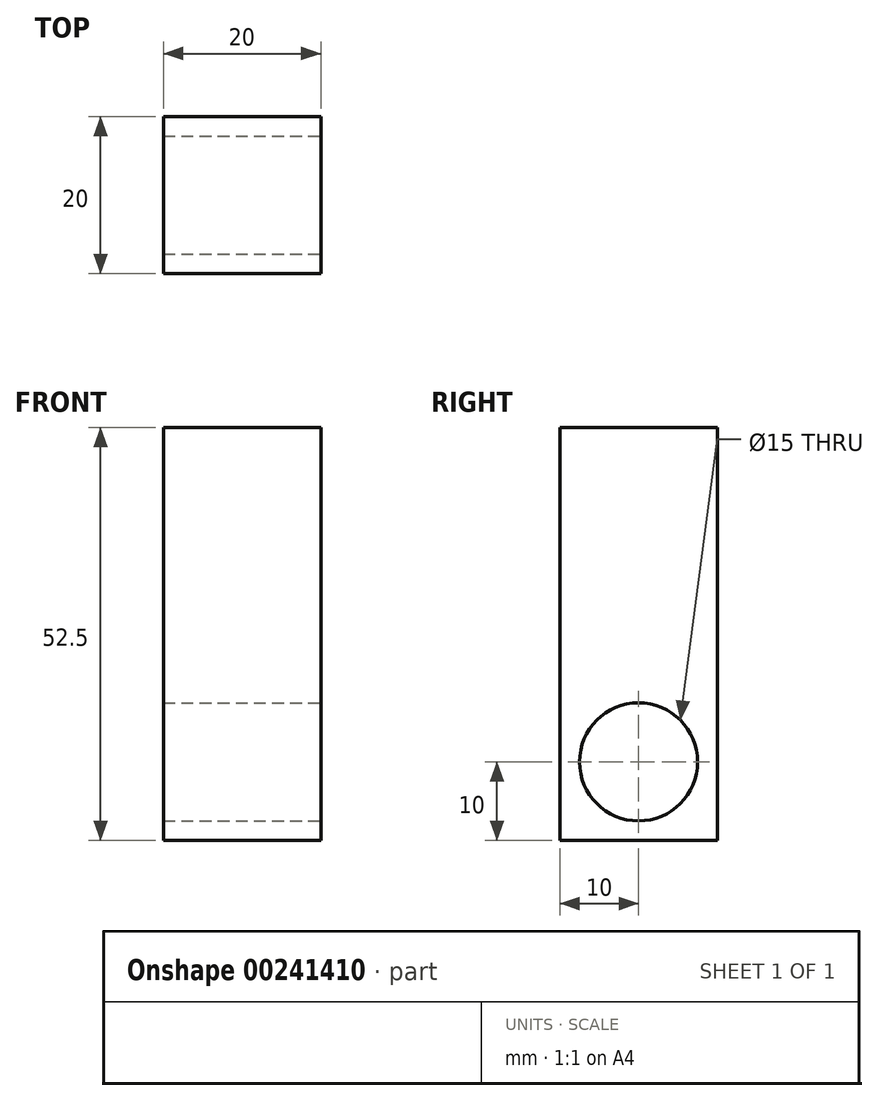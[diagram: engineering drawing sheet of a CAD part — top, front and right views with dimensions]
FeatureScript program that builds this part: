
annotation { "Feature Type Name" : "Feature", "Feature Type Description" : "" }
export const myFeature = defineFeature(function(context is Context, id is Id, definition is map)
    precondition{}
    {
        {
            var Q0;
            Q0=qCreatedBy(makeId("Right.planeOp"),FACE);
            var sketch = newSketch(context, id + "F0", { "sketchPlane" : qUnion([Q0])});
            skLineSegment(sketch, "E0.bottom", {"start": v(-10, 10) * mm, "end": v(10, 10) * mm});
            skLineSegment(sketch, "E0.top", {"start": v(-10, -10) * mm, "end": v(10, -10) * mm});
            skLineSegment(sketch, "E0.left", {"start": v(-10, 10) * mm, "end": v(-10, -10) * mm});
            skLineSegment(sketch, "E0.right", {"start": v(10, 10) * mm, "end": v(10, -10) * mm});
            skPoint(sketch, "E0.middle", {"position": v(0, 0) * mm});
            skSolve(sketch);
        }
        {
            var Q0;
            Q0 = qSketchRegion(id + "F0", true);
            extrude(context, id + "F1", {"entities" : qUnion([Q0]), "depth" : 20 * mm});
        }
        {
            var Q0;
            Q0=makeQuery(id+"F1.opExtrude","CAP_FACE",FACE,{"disambiguationData":[OSD([sQuery(id+"F0.wireOp",EDGE,"E0.bottom"),sQuery(id+"F0.wireOp",EDGE,"E0.top"),sQuery(id+"F0.wireOp",EDGE,"E0.left"),sQuery(id+"F0.wireOp",EDGE,"E0.right")])],"isStart":false});
            var sketch = newSketch(context, id + "F2", { "sketchPlane" : qUnion([Q0])});
            skCircle(sketch, "E1", {"center": v(0, 0) * mm, "radius": 7.5 * mm});
            skSolve(sketch);
        }
        {
            var Q0;
            Q0 = qSketchRegion(id + "F2", true);
            extrude(context, id + "F3", {"entities" : qUnion([Q0]), "operationType" : NewBodyOperationType.REMOVE, "endBound" : BoundingType.THROUGH_ALL, "oppositeDirection" : true, "depth" : 10 * mm});
        }
        {
            var Q0;
            Q0=makeQuery(id+"F1.opExtrude","SWEPT_FACE",FACE,{"disambiguationData":[OSD([sQuery(id+"F0.wireOp",EDGE,"E0.bottom")])]});
            var sketch = newSketch(context, id + "F4", { "sketchPlane" : qUnion([Q0])});
            skLineSegment(sketch, "E2.bottom", {"start": v(20, 10) * mm, "end": v(0, 10) * mm});
            skLineSegment(sketch, "E2.top", {"start": v(20, -10) * mm, "end": v(0, -10) * mm});
            skLineSegment(sketch, "E2.left", {"start": v(20, 10) * mm, "end": v(20, -10) * mm});
            skLineSegment(sketch, "E2.right", {"start": v(0, 10) * mm, "end": v(0, -10) * mm});
            skPoint(sketch, "E2.middle", {"position": v(10, 0) * mm});
            skPoint(sketch, "E2.middle.positionSnap0", {"position": v(10, 10) * mm});
            skPoint(sketch, "E2.middle.positionSnap1", {"position": v(20, 0) * mm});
            skPoint(sketch, "E2.centerSnap0", {"position": v(10, 10) * mm});
            skPoint(sketch, "E2.centerSnap1", {"position": v(20, 0) * mm});
            skSolve(sketch);
        }
        {
            var Q0;
            Q0 = qSketchRegion(id + "F4", true);
            extrude(context, id + "F5", {"entities" : qUnion([Q0]), "operationType" : NewBodyOperationType.ADD, "depth" : 32.5 * mm});
        }
    });
